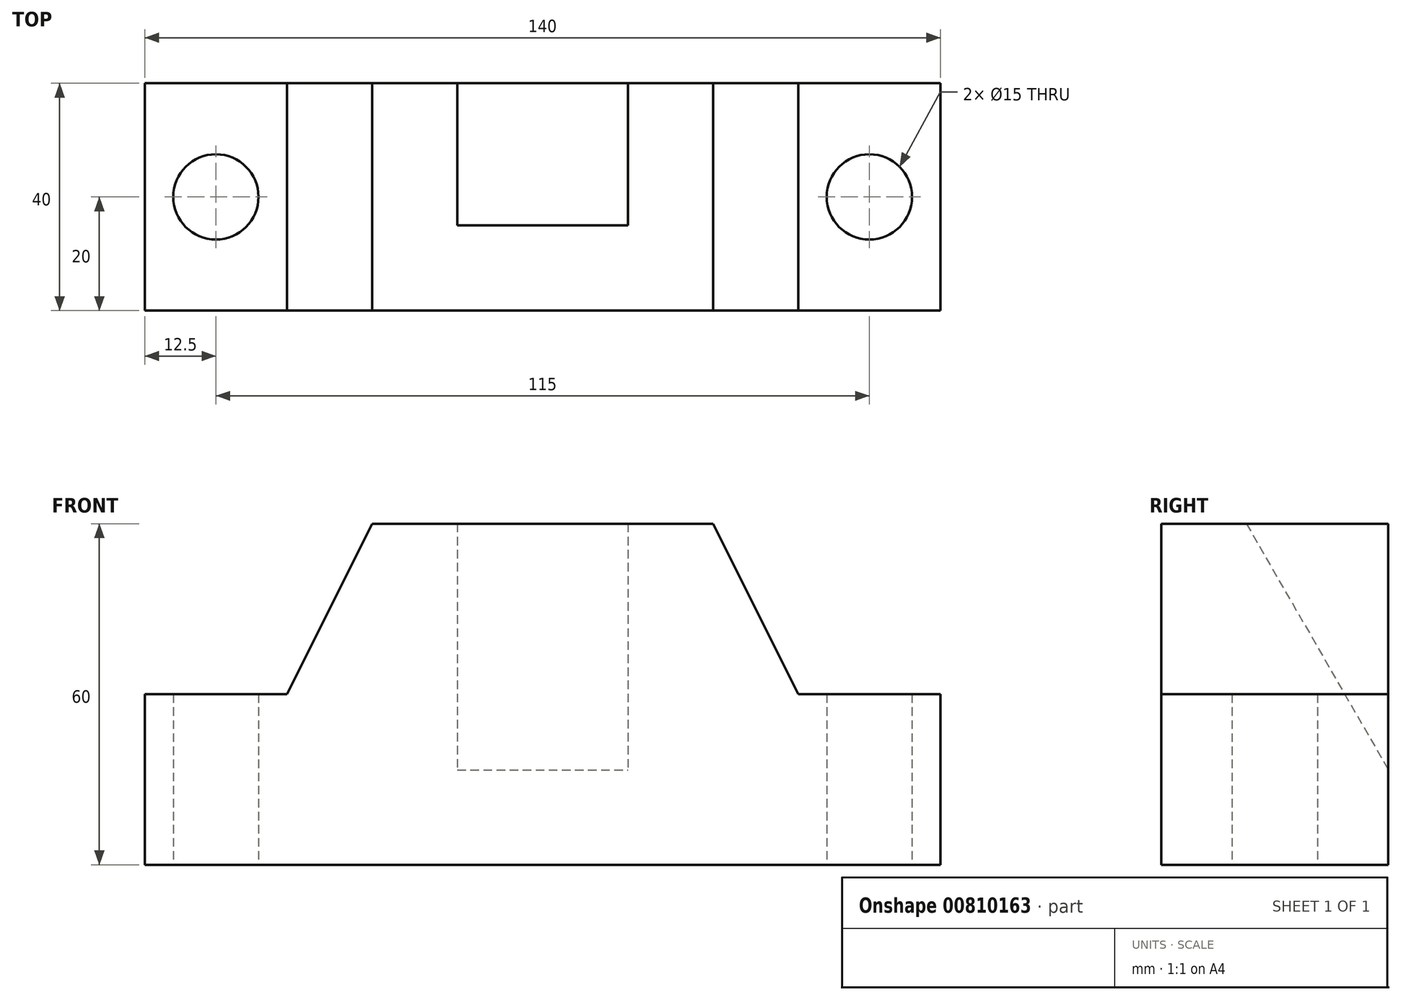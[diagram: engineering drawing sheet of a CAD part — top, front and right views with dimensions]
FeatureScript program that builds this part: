
annotation { "Feature Type Name" : "Feature", "Feature Type Description" : "" }
export const myFeature = defineFeature(function(context is Context, id is Id, definition is map)
    precondition{}
    {
        {
            var Q0;
            Q0=qCreatedBy(makeId("Front.planeOp"),FACE);
            var sketch = newSketch(context, id + "F0", { "sketchPlane" : qUnion([Q0])});
            skLineSegment(sketch, "E0", {"start": v(0, 0) * mm, "end": v(140, 0) * mm});
            skLineSegment(sketch, "E1", {"start": v(140, 0) * mm, "end": v(140, 30) * mm});
            skLineSegment(sketch, "E2", {"start": v(140, 30) * mm, "end": v(115, 30) * mm});
            skLineSegment(sketch, "E3", {"start": v(0, 0) * mm, "end": v(0, 30) * mm});
            skLineSegment(sketch, "E4", {"start": v(0, 30) * mm, "end": v(25, 30) * mm});
            skLineSegment(sketch, "E5", {"start": v(40, 60) * mm, "end": v(25, 30) * mm});
            skLineSegment(sketch, "E6", {"start": v(100, 60) * mm, "end": v(115, 30) * mm});
            skLineSegment(sketch, "E7", {"start": v(40, 60) * mm, "end": v(55, 60) * mm});
            skLineSegment(sketch, "E8", {"start": v(100, 60) * mm, "end": v(85, 60) * mm});
            skLineSegment(sketch, "E9", {"start": v(85, 60) * mm, "end": v(55, 60) * mm});
            skSolve(sketch);
        }
        {
            var Q0;
            Q0=makeQuery(id+"F0.imprint","IMPRINT",FACE,{"disambiguationData":[TD([[makeQuery(id+"F0.imprint","IMPRINT",EDGE,{"derivedFrom":sQuery(id+"F0.wireOp",EDGE,"E0")}),1.0]])]});
            extrude(context, id + "F1", {"entities" : qUnion([Q0]), "depth" : 40 * mm, "offsetDistance" : 25 * mm});
        }
        {
            var Q0;
            Q0=qCreatedBy(makeId("Front.planeOp"),FACE);
            var sketch = newSketch(context, id + "F2", { "sketchPlane" : qUnion([Q0])});
            skLineSegment(sketch, "E10.bottom", {"start": v(55, 60) * mm, "end": v(85, 60) * mm});
            skLineSegment(sketch, "E10.top", {"start": v(55, 15) * mm, "end": v(85, 15) * mm});
            skLineSegment(sketch, "E10.left", {"start": v(55, 60) * mm, "end": v(55, 15) * mm});
            skLineSegment(sketch, "E10.right", {"start": v(85, 60) * mm, "end": v(85, 15) * mm});
            skSolve(sketch);
        }
        {
            var Q0;
            Q0 = qSketchRegion(id + "F2", true);
            extrude(context, id + "F3", {"entities" : qUnion([Q0]), "operationType" : NewBodyOperationType.REMOVE, "depth" : 25 * mm, "offsetDistance" : 25 * mm});
        }
        {
            var Q0;
            Q0=makeQuery(id+"F3.boolean.opBoolean","COPY",EDGE,{"derivedFrom":makeQuery(id+"F3.opExtrude","CAP_EDGE",EDGE,{"disambiguationData":[OSD([sQuery(id+"F2.wireOp",EDGE,"E10.top")])],"isStart":false})});
            chamfer(context, id + "F4", {"entities" : qUnion([Q0]), "chamferType" : ChamferType.OFFSET_ANGLE, "width" : 45 * mm, "oppositeDirection" : true, "angle" : 30 * degree, "tangentPropagation" : true});
        }
        {
            var Q0;
            Q0=qCreatedBy(makeId("Top.planeOp"),FACE);
            var sketch = newSketch(context, id + "F5", { "sketchPlane" : qUnion([Q0])});
            skCircle(sketch, "E11", {"center": v(12.5, -20) * mm, "radius": 7.5 * mm});
            skLineSegment(sketch, "E12", {"start": v(0, 0) * mm, "end": v(12.5, 0) * mm});
            skLineSegment(sketch, "E13", {"start": v(12.5, 0) * mm, "end": v(12.5, -20) * mm});
            skCircle(sketch, "E14", {"center": v(127.5, -20) * mm, "radius": 7.5 * mm});
            skSolve(sketch);
        }
        {
            var Q0;
            Q0=makeQuery(id+"F5.imprint","IMPRINT",FACE,{"disambiguationData":[TD([[makeQuery(id+"F5.imprint","IMPRINT",EDGE,{"derivedFrom":sQuery(id+"F5.wireOp",EDGE,"E14")}),1.0]])]});
            var Q1;
            Q1=makeQuery(id+"F5.imprint","IMPRINT",FACE,{"disambiguationData":[TD([[makeQuery(id+"F5.imprint","IMPRINT",EDGE,{"derivedFrom":sQuery(id+"F5.wireOp",EDGE,"E11")}),1.0]])]});
            var Q2;
            Q2=sQuery(id+"F5.wireOp",EDGE,"E11");
            extrude(context, id + "F6", {"entities" : qUnion([Q0, Q1]), "operationType" : NewBodyOperationType.REMOVE, "surfaceEntities" : qUnion([Q2]), "depth" : 30 * mm, "offsetDistance" : 25 * mm});
        }
    });
